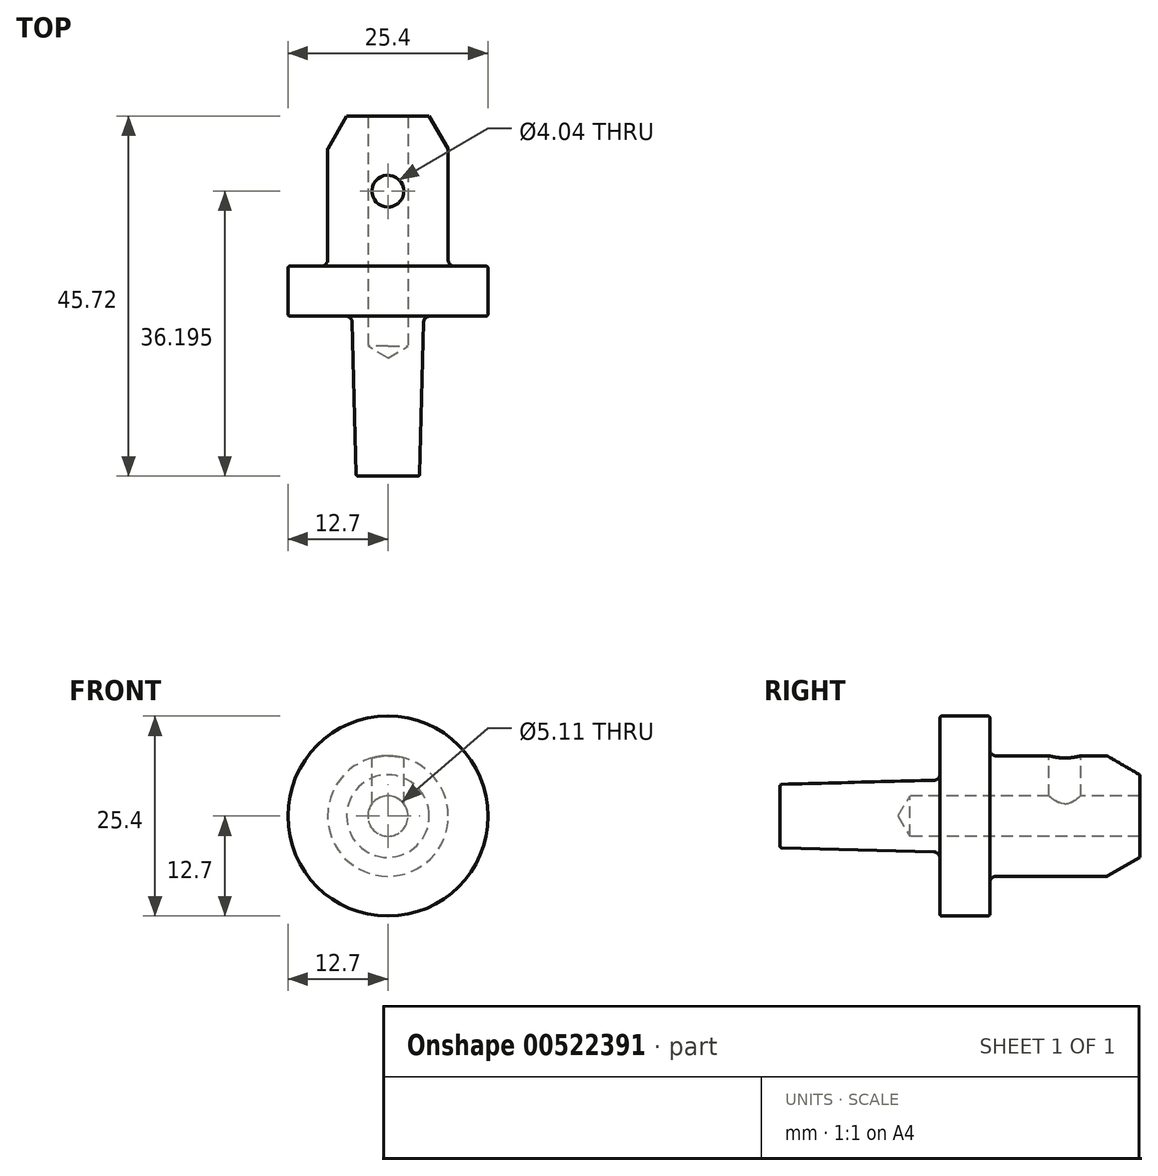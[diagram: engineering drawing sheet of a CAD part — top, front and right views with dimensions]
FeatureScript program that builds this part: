
annotation { "Feature Type Name" : "Feature", "Feature Type Description" : "" }
export const myFeature = defineFeature(function(context is Context, id is Id, definition is map)
    precondition{}
    {
        {
            var Q0;
            Q0=qCreatedBy(makeId("Right.planeOp"),FACE);
            var sketch = newSketch(context, id + "F0", { "sketchPlane" : qUnion([Q0])});
            skLineSegment(sketch, "E0", {"start": v(25.4, 0) * mm, "end": v(25.4, 12.7) * mm});
            skLineSegment(sketch, "E1", {"start": v(25.4, 12.7) * mm, "end": v(0, 12.7) * mm});
            skLineSegment(sketch, "E2", {"start": v(0, 12.7) * mm, "end": v(0, 4.57) * mm});
            skLineSegment(sketch, "E3", {"start": v(0, 4.57) * mm, "end": v(-20.32, 4.04) * mm});
            skLineSegment(sketch, "E4", {"start": v(-20.32, 4.04) * mm, "end": v(-20.32, 0) * mm});
            skLineSegment(sketch, "E5", {"start": v(-20.32, 0) * mm, "end": v(25.4, 0) * mm});
            skLineSegment(sketch, "E6", {"start": v(-47.9, 0) * mm, "end": v(43.15, 0) * mm, "construction": true});
            skSolve(sketch);
        }
        {
            var Q0;
            Q0=qSketchRegion(id+"F0",true);
            var Q1;
            Q1=sQuery(id+"F0.wireOp",EDGE,"E5");
            revolve(context, id + "F1", {"entities" : qUnion([Q0]), "axis" : qUnion([Q1]), "revolveType" : RevolveType.FULL});
        }
        {
            var Q0;
            Q0=makeQuery(id+"F1.opRevolve","SWEPT_EDGE",EDGE,{"disambiguationData":[OSD([sQuery(id+"F0.wireOp",EDGE,"E2"),sQuery(id+"F0.wireOp",EDGE,"E3")])]});
            fillet(context, id + "F2", {"entities" : qUnion([Q0]), "radius" : 0.76 * mm, "tangentPropagation" : true, "allowEdgeOverflow" : false});
        }
        {
            var Q0;
            Q0=makeQuery(id+"F1.opRevolve","SWEPT_EDGE",EDGE,{"disambiguationData":[OSD([sQuery(id+"F0.wireOp",EDGE,"E1"),sQuery(id+"F0.wireOp",EDGE,"E2")])]});
            var Q1;
            Q1=makeQuery(id+"F1.opRevolve","SWEPT_EDGE",EDGE,{"disambiguationData":[OSD([sQuery(id+"F0.wireOp",EDGE,"E0"),sQuery(id+"F0.wireOp",EDGE,"E1")])]});
            var Q2;
            Q2=makeQuery(id+"F1.opRevolve","SWEPT_EDGE",EDGE,{"disambiguationData":[OSD([sQuery(id+"F0.wireOp",EDGE,"E3"),sQuery(id+"F0.wireOp",EDGE,"E4")])]});
            fillet(context, id + "F3", {"entities" : qUnion([Q0, Q1, Q2]), "radius" : 0.25 * mm, "tangentPropagation" : true, "allowEdgeOverflow" : false});
        }
        {
            var Q0;
            Q0=qCreatedBy(makeId("Right.planeOp"),FACE);
            var sketch = newSketch(context, id + "F4", { "sketchPlane" : qUnion([Q0])});
            skLineSegment(sketch, "E7", {"start": v(-51.53, 0) * mm, "end": v(59.6, 0) * mm, "construction": true});
            skLineSegment(sketch, "E8", {"start": v(6.35, 19.05) * mm, "end": v(6.35, 7.66) * mm});
            skLineSegment(sketch, "E9", {"start": v(6.35, 7.66) * mm, "end": v(21.22, 7.66) * mm});
            skLineSegment(sketch, "E10", {"start": v(21.22, 7.66) * mm, "end": v(25.4, 5.24) * mm});
            skLineSegment(sketch, "E11", {"start": v(25.4, 5.24) * mm, "end": v(25.4, 19.05) * mm});
            skLineSegment(sketch, "E12", {"start": v(25.4, 19.05) * mm, "end": v(6.35, 19.05) * mm});
            skLineSegment(sketch, "E13", {"start": v(-3.93, 2.55) * mm, "end": v(30.6, 2.55) * mm, "construction": true});
            skSolve(sketch);
        }
        {
            var Q0;
            Q0 = qSketchRegion(id + "F4", true);
            var Q1;
            Q1=sQuery(id+"F4.wireOp",EDGE,"E7");
            revolve(context, id + "F5", {"operationType" : NewBodyOperationType.REMOVE, "entities" : qUnion([Q0]), "axis" : qUnion([Q1]), "revolveType" : RevolveType.FULL, "oppositeDirection" : true});
        }
        {
            var Q0;
            Q0=makeQuery(id+"F5.boolean.opBoolean","COPY",EDGE,{"derivedFrom":makeQuery(id+"F5.opRevolve","SWEPT_EDGE",EDGE,{"disambiguationData":[OSD([sQuery(id+"F4.wireOp",EDGE,"E8"),sQuery(id+"F4.wireOp",EDGE,"E9")])]})});
            fillet(context, id + "F6", {"entities" : qUnion([Q0]), "radius" : 0.76 * mm, "tangentPropagation" : true, "allowEdgeOverflow" : false});
        }
        {
            var Q0;
            Q0=makeQuery(id+"F5.boolean.opBoolean","INTERSECT",EDGE,{"derivedFrom":[makeQuery(id+"F1.opRevolve","SWEPT_FACE",FACE,{"disambiguationData":[OSD([sQuery(id+"F0.wireOp",EDGE,"E1")])]}),makeQuery(id+"F5.opRevolve","SWEPT_FACE",FACE,{"disambiguationData":[OSD([sQuery(id+"F4.wireOp",EDGE,"E8")])]})]});
            var Q1;
            Q1=makeQuery(id+"F5.boolean.opBoolean","COPY",EDGE,{"derivedFrom":makeQuery(id+"F5.opRevolve","SWEPT_EDGE",EDGE,{"disambiguationData":[OSD([sQuery(id+"F4.wireOp",EDGE,"E9"),sQuery(id+"F4.wireOp",EDGE,"E10")])]})});
            var Q2;
            Q2=makeQuery(id+"F5.boolean.opBoolean","COPY",EDGE,{"derivedFrom":makeQuery(id+"F5.opRevolve","SWEPT_EDGE",EDGE,{"disambiguationData":[OSD([sQuery(id+"F4.wireOp",EDGE,"E10"),sQuery(id+"F4.wireOp",EDGE,"E11")])]})});
            fillet(context, id + "F7", {"entities" : qUnion([Q0, Q1, Q2]), "radius" : 0.25 * mm, "tangentPropagation" : true, "allowEdgeOverflow" : false});
        }
        {
            var Q0;
            Q0=makeQuery(id+"F1.opRevolve","SWEPT_FACE",FACE,{"disambiguationData":[OSD([sQuery(id+"F0.wireOp",EDGE,"E0")])]});
            var sketch = newSketch(context, id + "F8", { "sketchPlane" : qUnion([Q0])});
            skPoint(sketch, "E14", {"position": v(0, 0) * mm});
            skSolve(sketch);
        }
        {
            var Q0;
            Q0=sQuery(id+"F8.wireOp",VERTEX,"E14");
            var Q1;
            Q1=makeQuery(id+"F1.opRevolve","SWEPT_BODY",BODY,{"disambiguationData":[OSD([sQuery(id+"F0.wireOp",EDGE,"E0"),sQuery(id+"F0.wireOp",EDGE,"E1"),sQuery(id+"F0.wireOp",EDGE,"E2"),sQuery(id+"F0.wireOp",EDGE,"E3"),sQuery(id+"F0.wireOp",EDGE,"E4"),sQuery(id+"F0.wireOp",EDGE,"E5")])]});
            hole(context, id + "F9", {"style" : HoleStyle.SIMPLE, "endStyle" : HoleEndStyle.BLIND, "standardTappedOrClearance" : lookupTablePath({ "standard" : "ANSI", "size" : "#7 (0.2)", "type" : "Drilled" }), "standardBlindInLast" : lookupTablePath({ "standard" : "ANSI", "size" : "#7", "type" : "Drilled" }), "holeDiameter" : 5.1 * mm, "holeDepth" : 29.2 * mm, "isTappedThrough" : true, "tappedDepth" : 18.41 * mm, "tapClearance" : 3, "startFromSketch" : true, "locations" : qUnion([Q0]), "scope" : qUnion([Q1])});
        }
        {
            var Q0;
            Q0=qCreatedBy(makeId("Top.planeOp"),FACE);
            var sketch = newSketch(context, id + "F10", { "sketchPlane" : qUnion([Q0])});
            skLineSegment(sketch, "E15", {"start": v(0, 45.8) * mm, "end": v(0, -30.53) * mm, "construction": true});
            skPoint(sketch, "E16", {"position": v(0, 15.87) * mm});
            skSolve(sketch);
        }
        {
            var Q0;
            Q0=sQuery(id+"F10.wireOp",VERTEX,"E16");
            var Q1;
            Q1=makeQuery(id+"F1.opRevolve","SWEPT_BODY",BODY,{"disambiguationData":[OSD([sQuery(id+"F0.wireOp",EDGE,"E0"),sQuery(id+"F0.wireOp",EDGE,"E1"),sQuery(id+"F0.wireOp",EDGE,"E2"),sQuery(id+"F0.wireOp",EDGE,"E3"),sQuery(id+"F0.wireOp",EDGE,"E4"),sQuery(id+"F0.wireOp",EDGE,"E5")])]});
            hole(context, id + "F11", {"style" : HoleStyle.SIMPLE, "endStyle" : HoleEndStyle.BLIND, "oppositeDirection" : true, "standardTappedOrClearance" : lookupTablePath({ "standard" : "ANSI", "engagement" : "75%", "pitch" : "32 tpi", "size" : "#10", "type" : "Tapped" }), "standardBlindInLast" : lookupTablePath({ "standard" : "ANSI", "engagement" : "75%", "pitch" : "32 tpi", "size" : "#10", "type" : "Tapped" }), "holeDiameter" : 4.04 * mm, "showTappedDepth" : true, "holeDepth" : 20.8 * mm, "isTappedThrough" : true, "tappedDepth" : 18.41 * mm, "tapClearance" : 3, "startFromSketch" : true, "locations" : qUnion([Q0]), "scope" : qUnion([Q1]), "majorDiameter" : 4.83 * mm});
        }
    });
